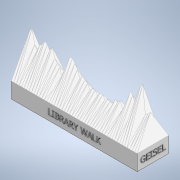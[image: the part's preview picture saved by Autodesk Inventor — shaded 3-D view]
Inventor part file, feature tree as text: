
AUTODESK INVENTOR PART (.ipt)
format: ipt  version: 2020.1 (Build 241239000, 239)  size: 1,908,736 bytes
history: native  units: in
note: dims shown in document units (in); Inventor stores cm internally (conversion verified against a paired STEP export)
features: extrude x5, sketch x5, projected_geometry x4, other x2
ambient origin geometry x8: Origin, YZ Plane, XZ Plane, XY Plane, X Axis, Y Axis, Z Axis, Center Point
bodies: Solid1 (feature_tree)
feature tree (16):
  other  "test"
  extrude  "Extrusion1"  Depth=8.0in
  extrude  "Extrusion2"  Depth=3.4972in
  extrude  "Extrusion3"  Depth=0.2391in
  extrude  "Extrusion4"  Depth=0.2in TaperAngle=0.0deg
  extrude  "Extrusion5"  Depth=0.2in
  sketch  "Sketch1"  dims[d0=1.0in d1=0.0in d2=8.0in]
  sketch  "Sketch2"  dims[d3=1.0in d4=3.4972in]
  projected_geometry  "Projected Loop1"
  sketch  "Sketch3"  dims[d5=0.5217in d6=0.2391in]
  projected_geometry  "Projected Loop2"
  sketch  "Sketch4"  dims[d7=2.2514in d8=0.2in d9=0.0in]
  projected_geometry  "Projected Loop3"
  sketch  "Sketch5"  dims[d10=8.0in d11=2.0in d12=3.1757in d13=0.9732in d14=4.0362in d15=1.7927in d16=0.1036in d17=0.5134in d18=0.2627in d19=0.2627in d20=0.2in d21=0.0in d22=2.0in d23=1.0in d24=1.5193in d25=0.7224in d26=0.2404in d27=0.1388in d28=0.2in d29=0.0in d30=8.0in d31=1.0in d32=6.53in d33=0.665in d34=0.735in d35=0.1675in d36=0.2in d37=0.0in]
  projected_geometry  "Projected Loop4"
  other  "MeshFeature1"
